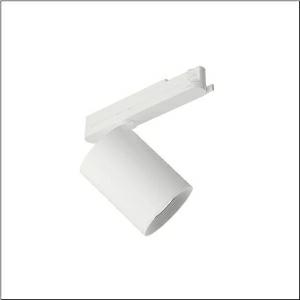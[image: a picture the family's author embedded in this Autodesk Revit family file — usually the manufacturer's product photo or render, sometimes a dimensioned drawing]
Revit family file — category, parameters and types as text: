
# Revit family: spot_21_51se14mbb5b
name_source: partatom
category: Lighting Fixtures
units: mm (PartAtom-declared; Revit-internal decimal feet)

## family parameters
Cut with Voids When Loaded = No
Host = Face
Light Source = No
Part Type = Normal
Room Calculation Point = No
Round Connector Dimension = Use Diameter
Shared = No

## types (1)
- --- (1 x LED, 5530 lm, 41.8 W, 3000K)
    Apparent Load = 42 VA
    CIE Flux Codes = 96 99 100 100 100
    Color Rendering = 90
    Color Temperature = 3000K
    Default Elevation = 1800 mm
    Description = Spot 21, directional spotlight, light control with lens, of PMMA, LED rated luminous flux: 5.110lm, light colour: 930, control gear: ECG Multilumen, with 3-phase adapter, mains connection: 220..240V, AC, 50/60Hz, of aluminium, traffic white (RAL 9016), length: 213mm, diameter: 105mm, protection rating (complete): IP20, insulation class (complete): insulation class I (protective earthing), certification: CE, impact resistance: IK02, permissible ambient temperature for indoor applications: -20..+40°C, packaging unit: 1 piece
    Height = 175 mm
    Lamp = 1 x LED
    Lamp Light Flux = 5530 lm
    Lamp Power = 41.8 W
    Lamp count = 1
    Length = 105 mm
    Luminous efficacy = 132 lm/W
    Manufacturer = Siteco
    ModVariant = No
    Model = 51SE14MBB5B
    Mounting Place = Ceiling
    Mounting Type = Pendant
    Number of Poles = 1
    OnlyDefault = Yes
    Power Factor = 1
    Product Name = Spot 21
    Product group = directional spotlight
    ProductGroupID = 905
    Protection Class = Protection class I
    Protection Degree = IP 20
    RLX_Detail_Level = 1
    RLX_Emergency_Light_Flux = 0 lm
    RLX_Emergency_Type = 0
    RLX_Emergency_Type_DB = No
    RlxData = <blob elided: 17657 chars, md5=8245bec3>
    Socket = socket
    Standby Power = 0 W
    System Light Flux = 5530 lm
    System Power = 42 W
    Type Comments = factory setting: luminous flux: 100 % | (ON | ON | ON | ON) | 1050 mA
    Type Image = l_1003976.jpg
    URL = http://relux.com
    VarID = @adj_143137
    Voltage = 0 V
    Weight = 0.00 kg
    Width = 0 mm  [stored 0 ft]

note: [stored X ft] marks values corroborated as IEEE doubles in the binary element streams (Revit-internal decimal feet)

## geometry (parser evidence)
native form markers: Blend x4, Sweep x9
no freeform markers — native parametric forms only
